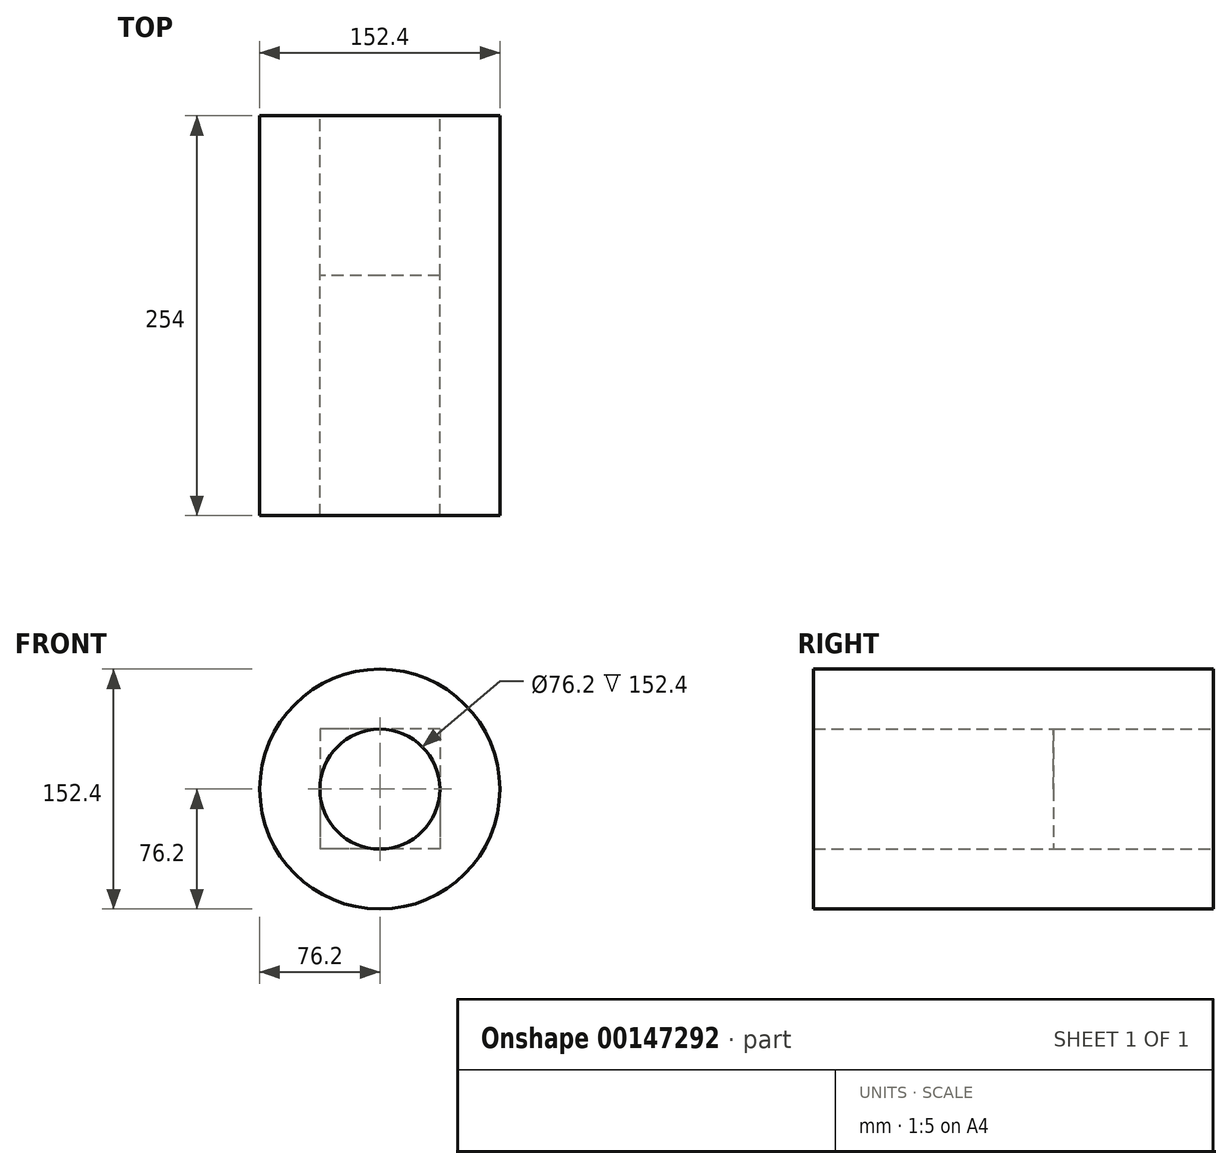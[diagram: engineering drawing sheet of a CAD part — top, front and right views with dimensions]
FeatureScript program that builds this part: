
annotation { "Feature Type Name" : "Feature", "Feature Type Description" : "" }
export const myFeature = defineFeature(function(context is Context, id is Id, definition is map)
    precondition{}
    {
        {
            var Q0;
            Q0=qCreatedBy(makeId("Front.planeOp"),FACE);
            var sketch = newSketch(context, id + "F0", { "sketchPlane" : qUnion([Q0])});
            skCircle(sketch, "E0", {"center": v(0, 0) * mm, "radius": 76.2 * mm});
            skSolve(sketch);
        }
        {
            var Q0;
            Q0=qCreatedBy(makeId("Front.planeOp"),FACE);
            var sketch = newSketch(context, id + "F1", { "sketchPlane" : qUnion([Q0])});
            skLineSegment(sketch, "E1.bottom", {"start": v(38.1, 38.1) * mm, "end": v(-38.1, 38.1) * mm});
            skLineSegment(sketch, "E1.top", {"start": v(38.1, -38.1) * mm, "end": v(-38.1, -38.1) * mm});
            skLineSegment(sketch, "E1.left", {"start": v(38.1, 38.1) * mm, "end": v(38.1, -38.1) * mm});
            skLineSegment(sketch, "E1.right", {"start": v(-38.1, 38.1) * mm, "end": v(-38.1, -38.1) * mm});
            skPoint(sketch, "E1.middle", {"position": v(0, 0) * mm});
            skCircle(sketch, "E2", {"center": v(0, 0) * mm, "radius": 38.1 * mm});
            skSolve(sketch);
        }
        {
            var Q0;
            Q0=makeQuery(id+"F0.imprint","IMPRINT",FACE,{"disambiguationData":[TD([[makeQuery(id+"F0.imprint","IMPRINT",EDGE,{"derivedFrom":sQuery(id+"F0.wireOp",EDGE,"E0")}),1.0]])]});
            extrude(context, id + "F2", {"entities" : qUnion([Q0]), "depth" : 254 * mm});
        }
        {
            var Q0;
            {var subQ0=sQuery(id+"F1.wireOp",EDGE,"E2");var subQ1=makeQuery(id+"F1.imprint","INTERSECT",VERTEX,{"derivedFrom":[sQuery(id+"F1.wireOp",EDGE,"E1.bottom"),subQ0]});Q0=makeQuery(id+"F1.imprint","IMPRINT",FACE,{"disambiguationData":[TD([[makeQuery(id+"F1.imprint","IMPRINT",EDGE,{"disambiguationData":[TD([[subQ1,1.0]])],"derivedFrom":subQ0}),1.0]])]});}
            extrude(context, id + "F3", {"entities" : qUnion([Q0]), "operationType" : NewBodyOperationType.REMOVE, "endBound" : BoundingType.THROUGH_ALL, "depth" : 25.4 * mm});
        }
        {
            var Q0;
            Q0 = qSketchRegion(id + "F1", true);
            extrude(context, id + "F4", {"entities" : qUnion([Q0]), "operationType" : NewBodyOperationType.REMOVE, "depth" : 101.6 * mm});
        }
    });
